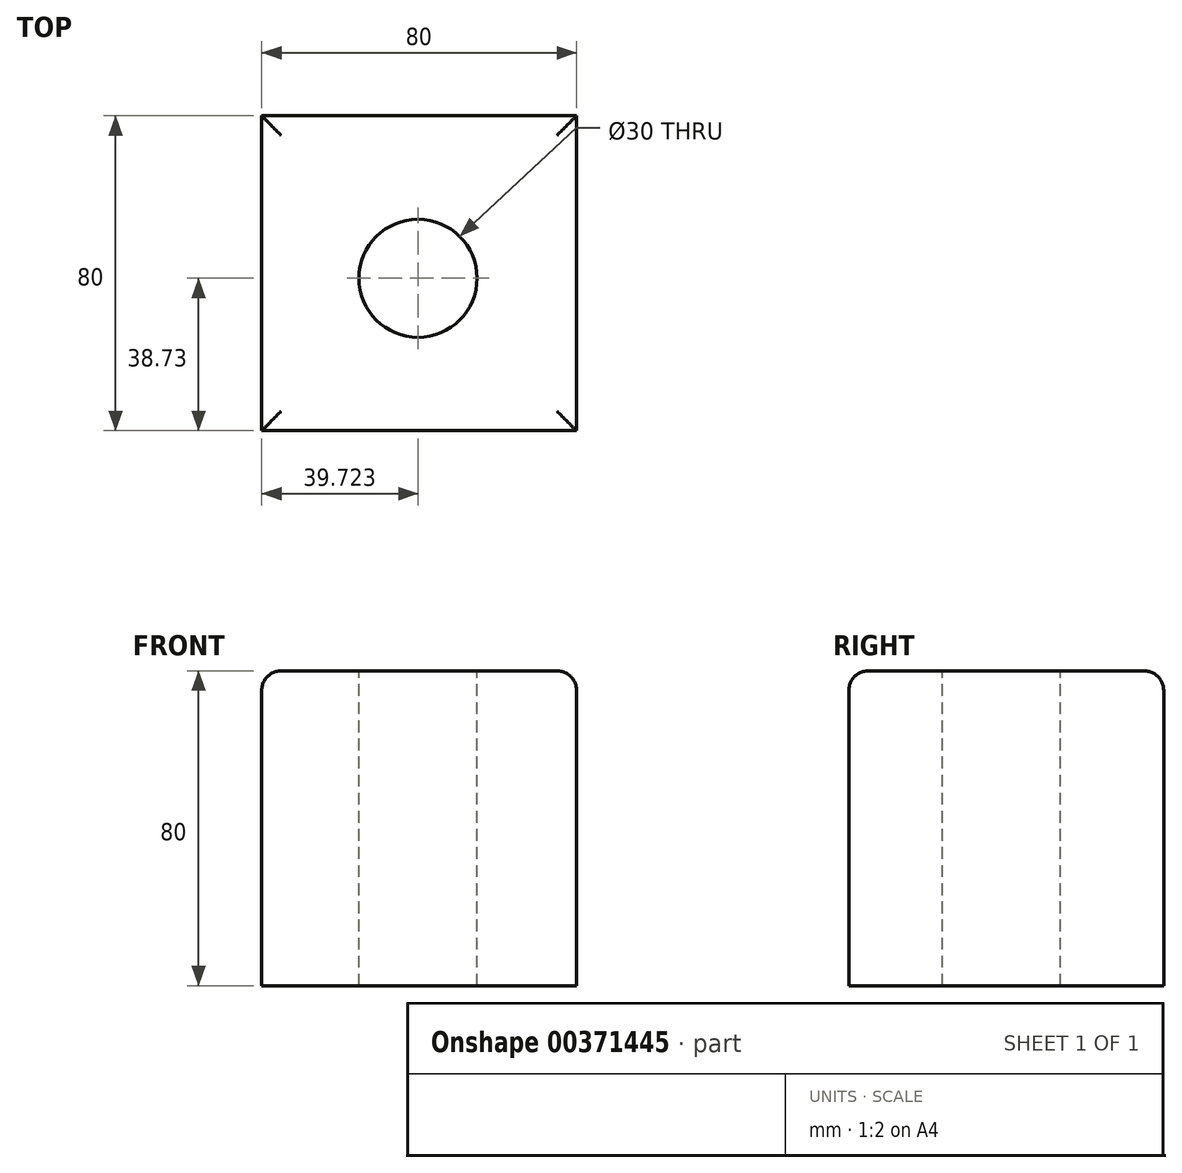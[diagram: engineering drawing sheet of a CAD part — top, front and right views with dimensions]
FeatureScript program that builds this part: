
annotation { "Feature Type Name" : "Feature", "Feature Type Description" : "" }
export const myFeature = defineFeature(function(context is Context, id is Id, definition is map)
    precondition{}
    {
        {
            var Q0;
            Q0=qCreatedBy(makeId("Top.planeOp"),FACE);
            var sketch = newSketch(context, id + "F0", { "sketchPlane" : qUnion([Q0])});
            skLineSegment(sketch, "E0.bottom", {"start": v(-126.25, 73.22) * mm, "end": v(-46.25, 73.22) * mm});
            skLineSegment(sketch, "E0.top", {"start": v(-126.25, -6.78) * mm, "end": v(-46.25, -6.78) * mm});
            skLineSegment(sketch, "E0.left", {"start": v(-126.25, 73.22) * mm, "end": v(-126.25, -6.78) * mm});
            skLineSegment(sketch, "E0.right", {"start": v(-46.25, 73.22) * mm, "end": v(-46.25, -6.78) * mm});
            skSolve(sketch);
        }
        {
            var Q0;
            Q0 = qSketchRegion(id + "F0", true);
            extrude(context, id + "F1", {"entities" : qUnion([Q0]), "depth" : 80 * mm});
        }
        {
            var Q0;
            Q0=makeQuery(id+"F1.opExtrude","CAP_FACE",FACE,{"disambiguationData":[OSD([sQuery(id+"F0.wireOp",EDGE,"E0.bottom"),sQuery(id+"F0.wireOp",EDGE,"E0.top"),sQuery(id+"F0.wireOp",EDGE,"E0.left"),sQuery(id+"F0.wireOp",EDGE,"E0.right")])],"isStart":false});
            var sketch = newSketch(context, id + "F2", { "sketchPlane" : qUnion([Q0])});
            skCircle(sketch, "E1", {"center": v(-86.53, 31.95) * mm, "radius": 15 * mm});
            skSolve(sketch);
        }
        {
            var Q0;
            Q0=makeQuery(id+"F2.imprint","IMPRINT",FACE,{"disambiguationData":[TD([[makeQuery(id+"F2.imprint","IMPRINT",EDGE,{"derivedFrom":sQuery(id+"F2.wireOp",EDGE,"E1")}),1.0]])]});
            extrude(context, id + "F3", {"entities" : qUnion([Q0]), "operationType" : NewBodyOperationType.REMOVE, "endBound" : BoundingType.THROUGH_ALL, "oppositeDirection" : true, "depth" : 25 * mm});
        }
        {
            var Q0;
            Q0=makeQuery(id+"F1.opExtrude","CAP_EDGE",EDGE,{"disambiguationData":[OSD([sQuery(id+"F0.wireOp",EDGE,"E0.bottom")])],"isStart":false});
            var Q1;
            Q1=makeQuery(id+"F1.opExtrude","CAP_EDGE",EDGE,{"disambiguationData":[OSD([sQuery(id+"F0.wireOp",EDGE,"E0.left")])],"isStart":false});
            var Q2;
            Q2=makeQuery(id+"F1.opExtrude","CAP_EDGE",EDGE,{"disambiguationData":[OSD([sQuery(id+"F0.wireOp",EDGE,"E0.top")])],"isStart":false});
            var Q3;
            Q3=makeQuery(id+"F1.opExtrude","CAP_EDGE",EDGE,{"disambiguationData":[OSD([sQuery(id+"F0.wireOp",EDGE,"E0.right")])],"isStart":false});
            fillet(context, id + "F4", {"entities" : qUnion([Q0, Q1, Q2, Q3]), "radius" : 5 * mm, "tangentPropagation" : true, "allowEdgeOverflow" : false});
        }
    });
